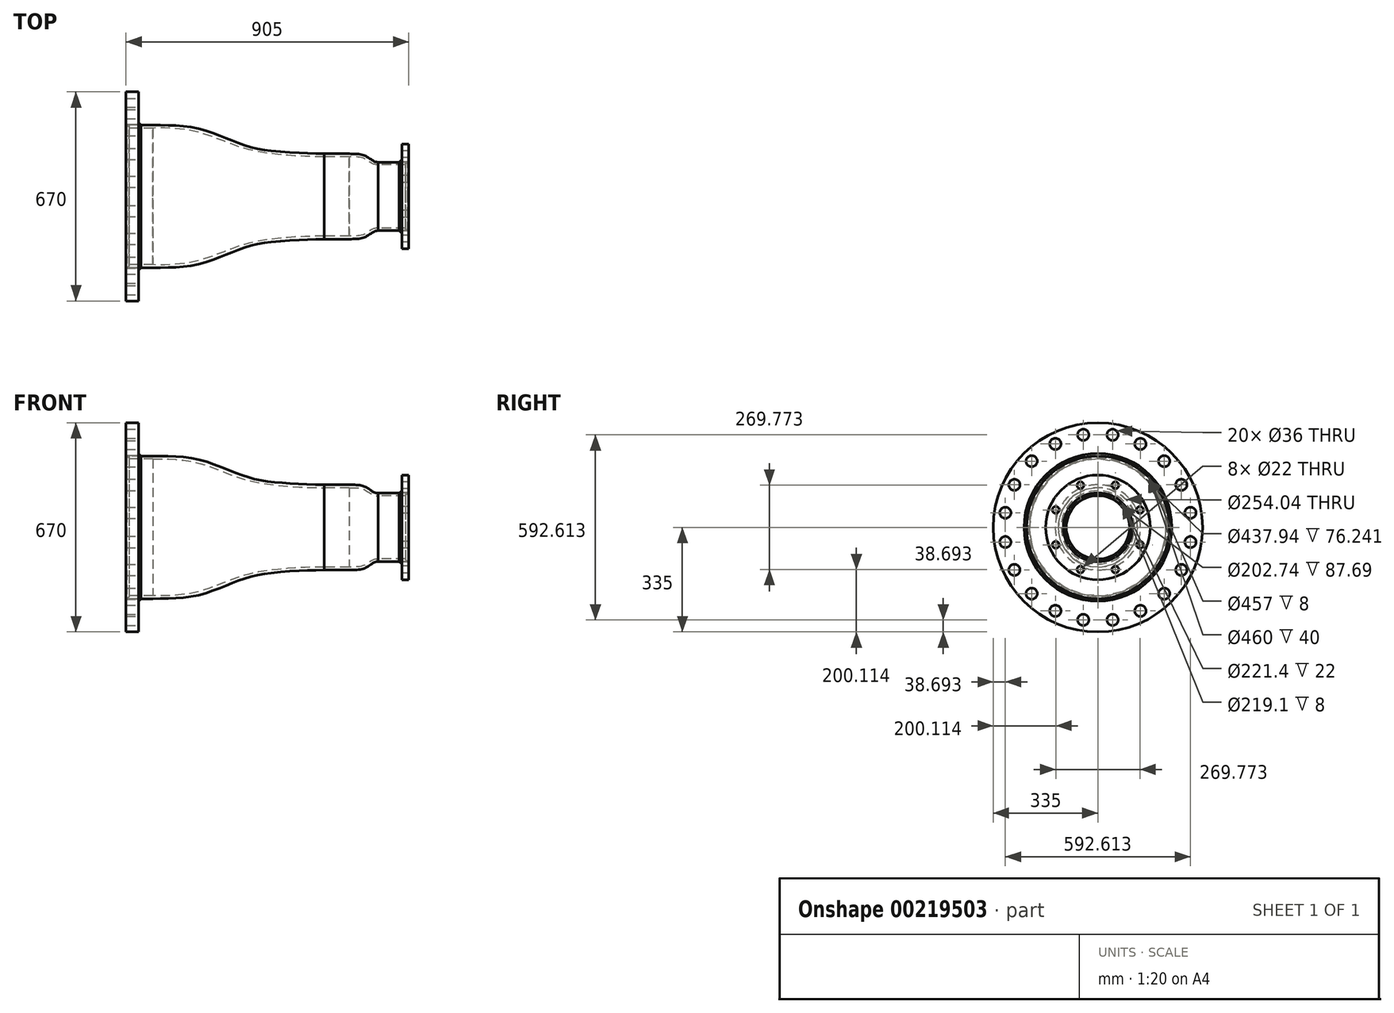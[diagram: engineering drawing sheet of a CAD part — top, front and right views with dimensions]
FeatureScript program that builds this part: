
annotation { "Feature Type Name" : "Feature", "Feature Type Description" : "" }
export const myFeature = defineFeature(function(context is Context, id is Id, definition is map)
    precondition{}
    {
        {
            var Q0;
            Q0=qCreatedBy(makeId("Front.planeOp"),FACE);
            var sketch = newSketch(context, id + "F0", { "sketchPlane" : qUnion([Q0])});
            skLineSegment(sketch, "E0", {"start": v(-562.58, 0) * mm, "end": v(652.64, 0) * mm, "construction": true});
            skLineSegment(sketch, "E1", {"start": v(-329.66, 228.5) * mm, "end": v(-253.37, 228.5) * mm});
            skLineSegment(sketch, "E2", {"start": v(375.34, 136.55) * mm, "end": v(295.32, 136.55) * mm});
            skFitSpline(sketch, "E3", {"points": [v(-253.37, 228.5) * mm, v(-109.72, 217.61) * mm, v(24.3, 169.13) * mm, v(129.85, 145.37) * mm, v(295.32, 136.55) * mm], "startDerivative": vector(539.24, -5.2) * mm, "endDerivative": vector(650.78, -14.67) * mm});
            skLineSegment(sketch, "E4.1", {"start": v(-329.66, 218.97) * mm, "end": v(-253.42, 218.97) * mm});
            skLineSegment(sketch, "E5.0", {"start": v(375.34, 127.02) * mm, "end": v(295.32, 127.02) * mm});
            skLineSegment(sketch, "E6", {"start": v(-329.66, 228.5) * mm, "end": v(-329.66, 218.97) * mm});
            skLineSegment(sketch, "E7", {"start": v(375.34, 136.55) * mm, "end": v(375.34, 127.02) * mm});
            skLineSegment(sketch, "E8.bottom", {"start": v(-299.66, 230) * mm, "end": v(-339.66, 230) * mm});
            skLineSegment(sketch, "E8.top", {"start": v(-299.66, 335) * mm, "end": v(-339.66, 335) * mm});
            skLineSegment(sketch, "E8.left", {"start": v(-299.66, 230) * mm, "end": v(-299.66, 335) * mm});
            skLineSegment(sketch, "E8.right", {"start": v(-339.66, 230) * mm, "end": v(-339.66, 335) * mm});
            skLineSegment(sketch, "E9", {"start": v(-299.66, 230) * mm, "end": v(-299.66, 228.5) * mm});
            skLineSegment(sketch, "E10", {"start": v(-337.66, 230) * mm, "end": v(-329.66, 222) * mm});
            skLineSegment(sketch, "E11", {"start": v(-299.66, 236.5) * mm, "end": v(-291.66, 228.5) * mm});
            skLineSegment(sketch, "E12", {"start": v(-329.66, 230) * mm, "end": v(-329.66, 228.5) * mm});
            skLineSegment(sketch, "E13", {"start": v(-253.37, 228.5) * mm, "end": v(-253.42, 218.97) * mm});
            skFitSpline(sketch, "E14", {"points": [v(-253.42, 218.97) * mm, v(-209.6, 218.97) * mm, v(-109.6, 206.39) * mm, v(24.68, 158.26) * mm, v(130.86, 136.31) * mm, v(236.57, 128.15) * mm, v(295.32, 127.02) * mm], "startDerivative": vector(341.33, 5.53) * mm, "endDerivative": vector(401.2, -2.2) * mm});
            skLineSegment(sketch, "E15", {"start": v(467.65, 109.55) * mm, "end": v(555.34, 109.55) * mm});
            skFitSpline(sketch, "E16", {"points": [v(375.34, 136.55) * mm, v(415.19, 133.8) * mm, v(432.68, 126.27) * mm, v(448.28, 116.32) * mm, v(467.65, 109.55) * mm], "startDerivative": vector(133.84, -0.21) * mm, "endDerivative": vector(156.27, -10.98) * mm});
            skLineSegment(sketch, "E17.0", {"start": v(467.65, 101.37) * mm, "end": v(555.34, 101.37) * mm});
            skLineSegment(sketch, "E18", {"start": v(555.34, 109.55) * mm, "end": v(555.34, 101.37) * mm});
            skLineSegment(sketch, "E19", {"start": v(467.65, 109.55) * mm, "end": v(467.65, 101.37) * mm});
            skFitSpline(sketch, "E20", {"points": [v(375.34, 127.02) * mm, v(389.62, 127.02) * mm, v(413.03, 124.71) * mm, v(426.2, 119.33) * mm, v(443.96, 108.57) * mm, v(456.34, 102.65) * mm, v(467.65, 101.37) * mm], "startDerivative": vector(82.33, 1.56) * mm, "endDerivative": vector(81.82, -3.15) * mm});
            skLineSegment(sketch, "E21.bottom", {"start": v(543.34, 110.7) * mm, "end": v(565.34, 110.7) * mm});
            skLineSegment(sketch, "E21.top", {"start": v(543.34, 167.5) * mm, "end": v(565.34, 167.5) * mm});
            skLineSegment(sketch, "E21.left", {"start": v(543.34, 110.7) * mm, "end": v(543.34, 167.5) * mm});
            skLineSegment(sketch, "E21.right", {"start": v(565.34, 110.7) * mm, "end": v(565.34, 167.5) * mm});
            skLineSegment(sketch, "E22", {"start": v(543.34, 110.7) * mm, "end": v(543.34, 109.55) * mm});
            skLineSegment(sketch, "E23", {"start": v(543.34, 117.55) * mm, "end": v(535.34, 109.55) * mm});
            skLineSegment(sketch, "E24", {"start": v(555.34, 110.7) * mm, "end": v(555.34, 109.55) * mm});
            skLineSegment(sketch, "E25", {"start": v(555.34, 102.7) * mm, "end": v(563.34, 110.7) * mm});
            skSolve(sketch);
        }
        {
            var Q0;
            {var subQ0=sQuery(id+"F0.wireOp",EDGE,"E8.top");Q0=makeQuery(id+"F0.imprint","IMPRINT",FACE,{"disambiguationData":[TD([[makeQuery(id+"F0.imprint","IMPRINT",EDGE,{"derivedFrom":subQ0}),1.0]])]});}
            var Q1;
            Q1=sQuery(id+"F0.wireOp",EDGE,"E0");
            revolve(context, id + "F1", {"entities" : qUnion([Q0]), "axis" : qUnion([Q1]), "revolveType" : RevolveType.FULL});
        }
        {
            var Q0;
            Q0=makeQuery(id+"F0.imprint","IMPRINT",FACE,{"disambiguationData":[TD([[makeQuery(id+"F0.imprint","IMPRINT",EDGE,{"derivedFrom":sQuery(id+"F0.wireOp",EDGE,"E3")}),-1.0]])]});
            var Q1;
            {var subQ0=sQuery(id+"F0.wireOp",EDGE,"E4.1");Q1=makeQuery(id+"F0.imprint","IMPRINT",FACE,{"disambiguationData":[TD([[makeQuery(id+"F0.imprint","IMPRINT",EDGE,{"derivedFrom":subQ0}),1.0]])]});}
            var Q2;
            {var subQ0=sQuery(id+"F0.wireOp",EDGE,"E5.0");Q2=makeQuery(id+"F0.imprint","IMPRINT",FACE,{"disambiguationData":[TD([[makeQuery(id+"F0.imprint","IMPRINT",EDGE,{"derivedFrom":subQ0}),-1.0]])]});}
            var Q3;
            Q3=sQuery(id+"F0.wireOp",EDGE,"E0");
            revolve(context, id + "F2", {"entities" : qUnion([Q0, Q1, Q2]), "axis" : qUnion([Q3]), "revolveType" : RevolveType.FULL});
        }
        {
            var Q0;
            {var subQ2=sQuery(id+"F0.wireOp",EDGE,"E10");Q0=makeQuery(id+"F0.imprint","IMPRINT",FACE,{"disambiguationData":[TD([[makeQuery(id+"F0.imprint","IMPRINT",EDGE,{"derivedFrom":subQ2}),1.0]])]});}
            var Q1;
            {var subQ0=sQuery(id+"F0.wireOp",EDGE,"E9");Q1=makeQuery(id+"F0.imprint","IMPRINT",FACE,{"disambiguationData":[TD([[makeQuery(id+"F0.imprint","IMPRINT",EDGE,{"derivedFrom":subQ0}),1.0]])]});}
            var Q2;
            {var subQ0=sQuery(id+"F0.wireOp",EDGE,"g5lh2SyO-cjbz-uzov-RsbH-qOUzou3A4Ysb");Q2=makeQuery(id+"F0.imprint","IMPRINT",FACE,{"disambiguationData":[TD([[makeQuery(id+"F0.imprint","IMPRINT",EDGE,{"derivedFrom":subQ0}),-1.0]])]});}
            var Q3;
            {var subQ0=sQuery(id+"F0.wireOp",EDGE,"kFAtr4YP-dI4c-IXYl-ZgJM-s1gs8BQtkOMe");Q3=makeQuery(id+"F0.imprint","IMPRINT",FACE,{"disambiguationData":[TD([[makeQuery(id+"F0.imprint","IMPRINT",EDGE,{"derivedFrom":subQ0}),1.0]])]});}
            var Q4;
            Q4=sQuery(id+"F0.wireOp",EDGE,"E0");
            revolve(context, id + "F3", {"entities" : qUnion([Q0, Q1, Q2, Q3]), "axis" : qUnion([Q4]), "revolveType" : RevolveType.FULL});
        }
        {
            var Q0;
            Q0=makeQuery(id+"F1.opRevolve","SWEPT_FACE",FACE,{"disambiguationData":[OSD([sQuery(id+"F0.wireOp",EDGE,"E8.right")])]});
            var sketch = newSketch(context, id + "F4", { "sketchPlane" : qUnion([Q0])});
            skCircle(sketch, "E26.cCircle", {"center": v(0, 0) * mm, "radius": 300 * mm, "construction": true});
            skLineSegment(sketch, "E26.0", {"start": v(212.13, 212.13) * mm, "end": v(267.3, 136.2) * mm});
            skLineSegment(sketch, "E26.1", {"start": v(267.3, 136.2) * mm, "end": v(296.3, 46.93) * mm});
            skLineSegment(sketch, "E26.2", {"start": v(296.3, 46.93) * mm, "end": v(296.3, -46.93) * mm});
            skLineSegment(sketch, "E26.3", {"start": v(296.3, -46.93) * mm, "end": v(267.3, -136.2) * mm});
            skLineSegment(sketch, "E26.4", {"start": v(267.3, -136.2) * mm, "end": v(212.13, -212.13) * mm});
            skLineSegment(sketch, "E26.5", {"start": v(212.13, -212.13) * mm, "end": v(136.2, -267.3) * mm});
            skLineSegment(sketch, "E26.6", {"start": v(136.2, -267.3) * mm, "end": v(46.93, -296.3) * mm});
            skLineSegment(sketch, "E26.7", {"start": v(46.93, -296.3) * mm, "end": v(-46.93, -296.3) * mm});
            skLineSegment(sketch, "E26.8", {"start": v(-46.93, -296.3) * mm, "end": v(-136.2, -267.3) * mm});
            skLineSegment(sketch, "E26.9", {"start": v(-136.2, -267.3) * mm, "end": v(-212.13, -212.13) * mm});
            skLineSegment(sketch, "E26.10", {"start": v(-212.13, -212.13) * mm, "end": v(-267.3, -136.2) * mm});
            skLineSegment(sketch, "E26.11", {"start": v(-267.3, -136.2) * mm, "end": v(-296.3, -46.93) * mm});
            skLineSegment(sketch, "E26.12", {"start": v(-296.3, -46.93) * mm, "end": v(-296.3, 46.93) * mm});
            skLineSegment(sketch, "E26.13", {"start": v(-296.3, 46.93) * mm, "end": v(-267.3, 136.2) * mm});
            skLineSegment(sketch, "E26.14", {"start": v(-267.3, 136.2) * mm, "end": v(-212.13, 212.13) * mm});
            skLineSegment(sketch, "E26.15", {"start": v(-212.13, 212.13) * mm, "end": v(-136.2, 267.3) * mm});
            skLineSegment(sketch, "E26.16", {"start": v(-136.2, 267.3) * mm, "end": v(-46.93, 296.3) * mm});
            skLineSegment(sketch, "E26.17", {"start": v(-46.93, 296.3) * mm, "end": v(46.93, 296.3) * mm});
            skLineSegment(sketch, "E26.18", {"start": v(46.93, 296.3) * mm, "end": v(136.2, 267.3) * mm});
            skLineSegment(sketch, "E26.19", {"start": v(136.2, 267.3) * mm, "end": v(212.13, 212.13) * mm});
            skPoint(sketch, "E27", {"position": v(-136.2, 267.3) * mm});
            skPoint(sketch, "E28", {"position": v(-46.93, 296.3) * mm});
            skPoint(sketch, "E29", {"position": v(46.93, 296.3) * mm});
            skPoint(sketch, "E30", {"position": v(136.2, 267.3) * mm});
            skPoint(sketch, "E31", {"position": v(212.13, 212.13) * mm});
            skPoint(sketch, "E32", {"position": v(267.3, 136.2) * mm});
            skPoint(sketch, "E33", {"position": v(296.3, 46.93) * mm});
            skPoint(sketch, "E34", {"position": v(296.3, -46.93) * mm});
            skPoint(sketch, "E35", {"position": v(267.3, -136.2) * mm});
            skPoint(sketch, "E36", {"position": v(212.13, -212.13) * mm});
            skPoint(sketch, "E37", {"position": v(136.2, -267.3) * mm});
            skPoint(sketch, "E38", {"position": v(46.93, -296.3) * mm});
            skPoint(sketch, "E39", {"position": v(-46.93, -296.3) * mm});
            skPoint(sketch, "E40", {"position": v(-136.2, -267.3) * mm});
            skPoint(sketch, "E41", {"position": v(-212.13, -212.13) * mm});
            skPoint(sketch, "E42", {"position": v(-267.3, -136.2) * mm});
            skPoint(sketch, "E43", {"position": v(-296.3, -46.93) * mm});
            skPoint(sketch, "E44", {"position": v(-296.3, 46.93) * mm});
            skPoint(sketch, "E45", {"position": v(-267.3, 136.2) * mm});
            skPoint(sketch, "E46", {"position": v(-212.13, 212.13) * mm});
            skSolve(sketch);
        }
        {
            var Q0;
            Q0=sQuery(id+"F4.wireOp",VERTEX,"E28");
            var Q1;
            Q1=sQuery(id+"F4.wireOp",VERTEX,"E29");
            var Q2;
            Q2=sQuery(id+"F4.wireOp",VERTEX,"E30");
            var Q3;
            Q3=sQuery(id+"F4.wireOp",VERTEX,"E31");
            var Q4;
            Q4=sQuery(id+"F4.wireOp",VERTEX,"E32");
            var Q5;
            Q5=sQuery(id+"F4.wireOp",VERTEX,"E33");
            var Q6;
            Q6=sQuery(id+"F4.wireOp",VERTEX,"E34");
            var Q7;
            Q7=sQuery(id+"F4.wireOp",VERTEX,"E35");
            var Q8;
            Q8=sQuery(id+"F4.wireOp",VERTEX,"E36");
            var Q9;
            Q9=sQuery(id+"F4.wireOp",VERTEX,"E37");
            var Q10;
            Q10=sQuery(id+"F4.wireOp",VERTEX,"E38");
            var Q11;
            Q11=sQuery(id+"F4.wireOp",VERTEX,"E40");
            var Q12;
            Q12=sQuery(id+"F4.wireOp",VERTEX,"E41");
            var Q13;
            Q13=sQuery(id+"F4.wireOp",VERTEX,"E42");
            var Q14;
            Q14=sQuery(id+"F4.wireOp",VERTEX,"E43");
            var Q15;
            Q15=sQuery(id+"F4.wireOp",VERTEX,"E39");
            var Q16;
            Q16=sQuery(id+"F4.wireOp",VERTEX,"E44");
            var Q17;
            Q17=sQuery(id+"F4.wireOp",VERTEX,"E45");
            var Q18;
            Q18=sQuery(id+"F4.wireOp",VERTEX,"E46");
            var Q19;
            Q19=sQuery(id+"F4.wireOp",VERTEX,"E27");
            var Q20;
            Q20=makeQuery(id+"F1.opRevolve","SWEPT_BODY",BODY,{"disambiguationData":[OSD([sQuery(id+"F0.wireOp",EDGE,"E8.bottom"),sQuery(id+"F0.wireOp",EDGE,"E8.top"),sQuery(id+"F0.wireOp",EDGE,"E8.left"),sQuery(id+"F0.wireOp",EDGE,"E8.right")])]});
            hole(context, id + "F5", {"style" : HoleStyle.SIMPLE, "endStyle" : HoleEndStyle.BLIND, "holeDiameter" : 36 * mm, "holeDepth" : 50 * mm, "locations" : qUnion([Q0, Q1, Q2, Q3, Q4, Q5, Q6, Q7, Q8, Q9, Q10, Q11, Q12, Q13, Q14, Q15, Q16, Q17, Q18, Q19]), "scope" : qUnion([Q20])});
        }
        {
            var Q0;
            Q0=makeQuery(id+"F0.imprint","IMPRINT",FACE,{"disambiguationData":[TD([[makeQuery(id+"F0.imprint","IMPRINT",EDGE,{"derivedFrom":sQuery(id+"F0.wireOp",EDGE,"E15")}),-1.0]])]});
            var Q1;
            Q1=makeQuery(id+"F0.imprint","IMPRINT",FACE,{"disambiguationData":[TD([[makeQuery(id+"F0.imprint","IMPRINT",EDGE,{"derivedFrom":sQuery(id+"F0.wireOp",EDGE,"E7")}),1.0]])]});
            var Q2;
            Q2=sQuery(id+"F0.wireOp",EDGE,"E0");
            revolve(context, id + "F6", {"operationType" : NewBodyOperationType.ADD, "entities" : qUnion([Q0, Q1]), "axis" : qUnion([Q2]), "revolveType" : RevolveType.FULL});
        }
        {
            var Q0;
            Q0=makeQuery(id+"F0.imprint","IMPRINT",FACE,{"disambiguationData":[TD([[makeQuery(id+"F0.imprint","IMPRINT",EDGE,{"derivedFrom":sQuery(id+"F0.wireOp",EDGE,"E21.bottom")}),1.0]])]});
            var Q1;
            Q1=sQuery(id+"F0.wireOp",EDGE,"E0");
            revolve(context, id + "F7", {"entities" : qUnion([Q0]), "axis" : qUnion([Q1]), "revolveType" : RevolveType.FULL});
        }
        {
            var Q0;
            {var subQ0=sQuery(id+"F0.wireOp",EDGE,"E22");Q0=makeQuery(id+"F0.imprint","IMPRINT",FACE,{"disambiguationData":[TD([[makeQuery(id+"F0.imprint","IMPRINT",EDGE,{"derivedFrom":subQ0}),-1.0]])]});}
            var Q1;
            {var subQ0=sQuery(id+"F0.wireOp",EDGE,"E24");Q1=makeQuery(id+"F0.imprint","IMPRINT",FACE,{"disambiguationData":[TD([[makeQuery(id+"F0.imprint","IMPRINT",EDGE,{"derivedFrom":subQ0}),1.0]])]});}
            var Q2;
            Q2=sQuery(id+"F0.wireOp",EDGE,"E0");
            revolve(context, id + "F8", {"entities" : qUnion([Q0, Q1]), "axis" : qUnion([Q2]), "revolveType" : RevolveType.FULL});
        }
        {
            var Q0;
            Q0=makeQuery(id+"F7.opRevolve","SWEPT_FACE",FACE,{"disambiguationData":[OSD([sQuery(id+"F0.wireOp",EDGE,"E21.right")])]});
            var sketch = newSketch(context, id + "F9", { "sketchPlane" : qUnion([Q0])});
            skCircle(sketch, "E47.cCircle", {"center": v(0, 0) * mm, "radius": 146 * mm, "construction": true});
            skLineSegment(sketch, "E47.0", {"start": v(-55.87, -134.89) * mm, "end": v(-134.89, -55.87) * mm});
            skLineSegment(sketch, "E47.1", {"start": v(-134.89, -55.87) * mm, "end": v(-134.89, 55.87) * mm});
            skLineSegment(sketch, "E47.2", {"start": v(-134.89, 55.87) * mm, "end": v(-55.87, 134.89) * mm});
            skLineSegment(sketch, "E47.3", {"start": v(-55.87, 134.89) * mm, "end": v(55.87, 134.89) * mm});
            skLineSegment(sketch, "E47.4", {"start": v(55.87, 134.89) * mm, "end": v(134.89, 55.87) * mm});
            skLineSegment(sketch, "E47.5", {"start": v(134.89, 55.87) * mm, "end": v(134.89, -55.87) * mm});
            skLineSegment(sketch, "E47.6", {"start": v(134.89, -55.87) * mm, "end": v(55.87, -134.89) * mm});
            skLineSegment(sketch, "E47.7", {"start": v(55.87, -134.89) * mm, "end": v(-55.87, -134.89) * mm});
            skPoint(sketch, "E48", {"position": v(134.89, 55.87) * mm});
            skPoint(sketch, "E49", {"position": v(134.89, -55.87) * mm});
            skPoint(sketch, "E50", {"position": v(55.87, -134.89) * mm});
            skPoint(sketch, "E51", {"position": v(-55.87, -134.89) * mm});
            skPoint(sketch, "E52", {"position": v(-134.89, -55.87) * mm});
            skPoint(sketch, "E53", {"position": v(-134.89, 55.87) * mm});
            skPoint(sketch, "E54", {"position": v(-55.87, 134.89) * mm});
            skPoint(sketch, "E55", {"position": v(55.87, 134.89) * mm});
            skSolve(sketch);
        }
        {
            var Q0;
            Q0=sQuery(id+"F9.wireOp",VERTEX,"E48");
            var Q1;
            Q1=sQuery(id+"F9.wireOp",VERTEX,"E49");
            var Q2;
            Q2=sQuery(id+"F9.wireOp",VERTEX,"E50");
            var Q3;
            Q3=sQuery(id+"F9.wireOp",VERTEX,"E51");
            var Q4;
            Q4=sQuery(id+"F9.wireOp",VERTEX,"E52");
            var Q5;
            Q5=sQuery(id+"F9.wireOp",VERTEX,"E53");
            var Q6;
            Q6=sQuery(id+"F9.wireOp",VERTEX,"E54");
            var Q7;
            Q7=sQuery(id+"F9.wireOp",VERTEX,"E55");
            var Q8;
            Q8=makeQuery(id+"F7.opRevolve","SWEPT_BODY",BODY,{"disambiguationData":[OSD([sQuery(id+"F0.wireOp",EDGE,"E21.bottom"),sQuery(id+"F0.wireOp",EDGE,"E21.top"),sQuery(id+"F0.wireOp",EDGE,"E21.left"),sQuery(id+"F0.wireOp",EDGE,"E21.right")])]});
            hole(context, id + "F10", {"style" : HoleStyle.SIMPLE, "endStyle" : HoleEndStyle.BLIND, "holeDiameter" : 22 * mm, "holeDepth" : 50 * mm, "locations" : qUnion([Q0, Q1, Q2, Q3, Q4, Q5, Q6, Q7]), "scope" : qUnion([Q8])});
        }
    });
